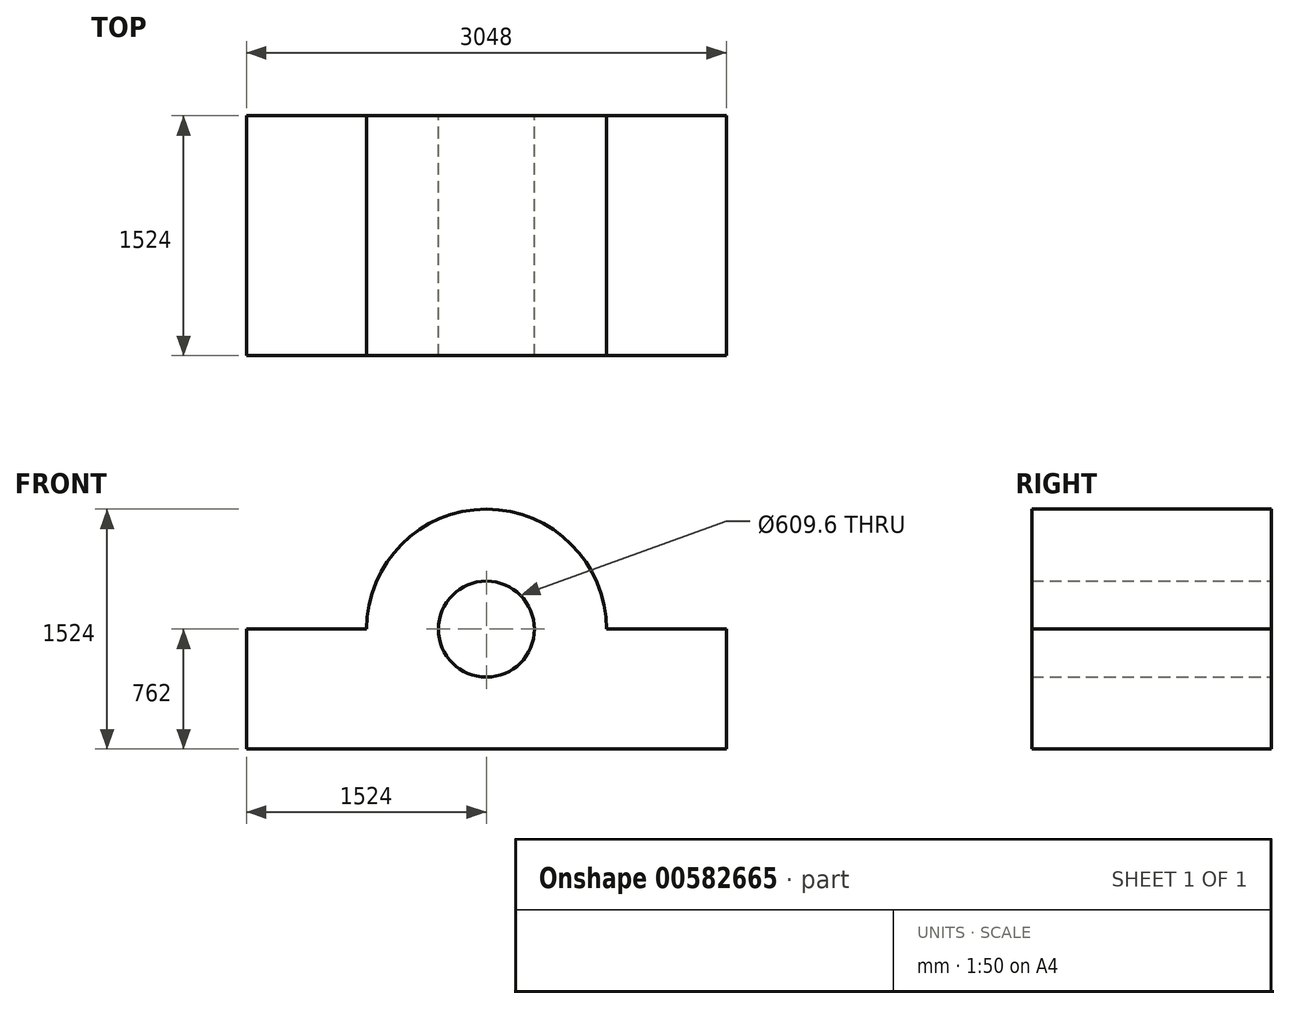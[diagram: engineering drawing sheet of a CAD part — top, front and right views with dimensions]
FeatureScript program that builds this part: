
annotation { "Feature Type Name" : "Feature", "Feature Type Description" : "" }
export const myFeature = defineFeature(function(context is Context, id is Id, definition is map)
    precondition{}
    {
        {
            var Q0;
            Q0=qCreatedBy(makeId("Front.planeOp"),FACE);
            var sketch = newSketch(context, id + "F0", { "sketchPlane" : qUnion([Q0])});
            skLineSegment(sketch, "E0", {"start": v(0, 0) * mm, "end": v(3048, 0) * mm});
            skLineSegment(sketch, "E1", {"start": v(3048, 0) * mm, "end": v(3048, 762) * mm});
            skLineSegment(sketch, "E2", {"start": v(3048, 762) * mm, "end": v(2286, 762) * mm});
            skLineSegment(sketch, "E3", {"start": v(0, 762) * mm, "end": v(0, 0) * mm});
            skCircle(sketch, "E4", {"center": v(1524, 762) * mm, "radius": 304.8 * mm});
            skArc(sketch, "E5", {"start": v(2286, 762) * mm, "mid": v(1524, 1524) * mm, "end": v(762, 762) * mm});
            skLineSegment(sketch, "E6.trimOffspring", {"start": v(762, 762) * mm, "end": v(0, 762) * mm});
            skSolve(sketch);
        }
        {
            var Q0;
            Q0=makeQuery(id+"F0.imprint","IMPRINT",FACE,{"disambiguationData":[TD([[makeQuery(id+"F0.imprint","IMPRINT",EDGE,{"derivedFrom":sQuery(id+"F0.wireOp",EDGE,"E0")}),1.0]])]});
            extrude(context, id + "F1", {"entities" : qUnion([Q0]), "depth" : 1524 * mm, "offsetDistance" : 25.4 * mm});
        }
    });
